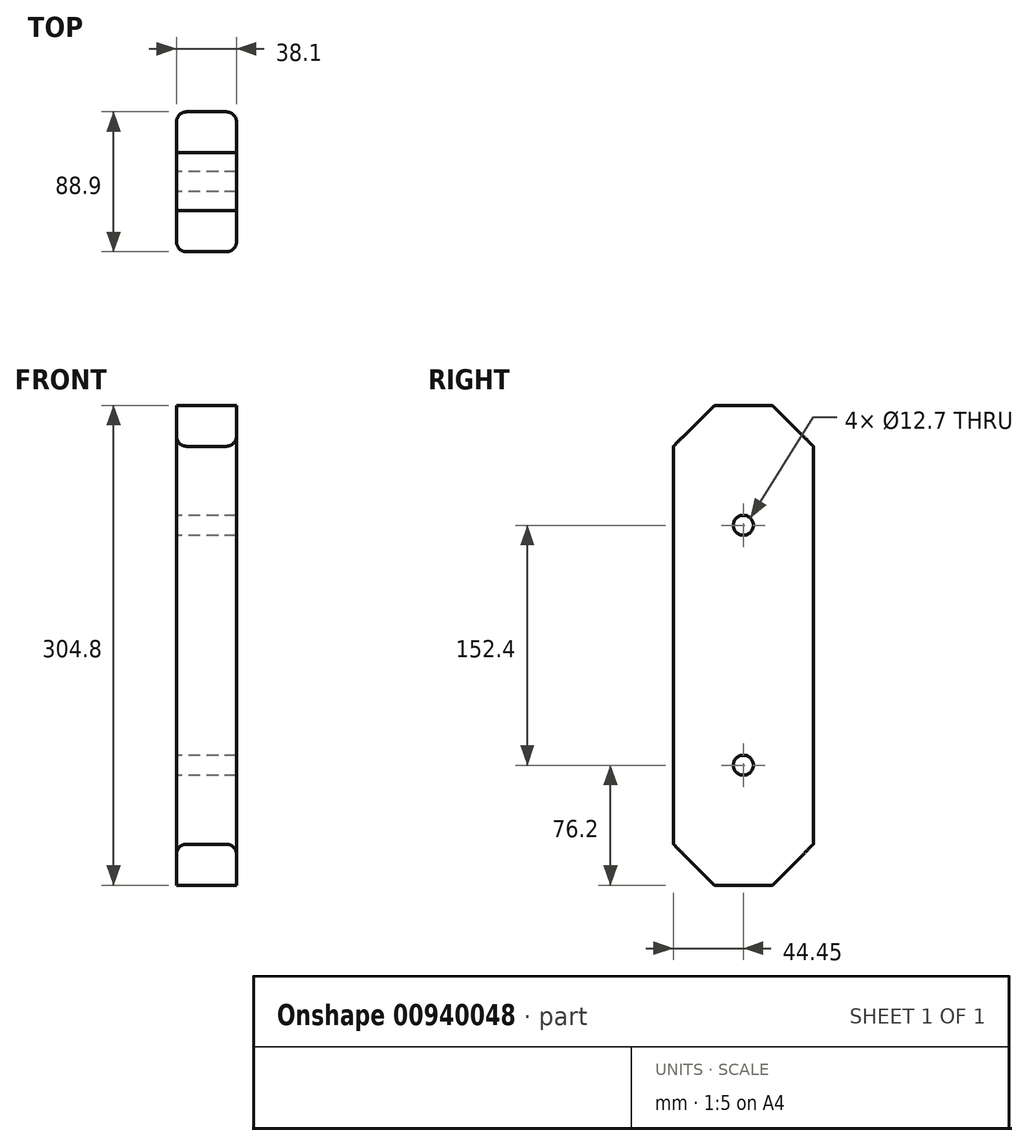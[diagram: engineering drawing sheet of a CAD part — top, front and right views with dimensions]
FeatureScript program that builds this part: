
annotation { "Feature Type Name" : "Feature", "Feature Type Description" : "" }
export const myFeature = defineFeature(function(context is Context, id is Id, definition is map)
    precondition{}
    {
        {
            var Q0;
            Q0=qCreatedBy(makeId("Top.planeOp"),FACE);
            var sketch = newSketch(context, id + "F0", { "sketchPlane" : qUnion([Q0])});
            skLineSegment(sketch, "E0.bottom", {"start": v(12.7, -44.45) * mm, "end": v(-12.7, -44.45) * mm});
            skLineSegment(sketch, "E0.top", {"start": v(12.7, 44.45) * mm, "end": v(-12.7, 44.45) * mm});
            skLineSegment(sketch, "E0.left", {"start": v(19.05, -38.1) * mm, "end": v(19.05, 38.1) * mm});
            skLineSegment(sketch, "E0.right", {"start": v(-19.05, -38.1) * mm, "end": v(-19.05, 38.1) * mm});
            skPoint(sketch, "E0.middle", {"position": v(0, 0) * mm});
            skPoint(sketch, "E1.visualSharp", {"position": v(19.05, -44.45) * mm});
            skArc(sketch, "E1.filletArc", {"start": v(12.7, -44.45) * mm, "mid": v(17.2, -42.6) * mm, "end": v(19.05, -38.1) * mm});
            skPoint(sketch, "E2.visualSharp", {"position": v(-19.05, -44.45) * mm});
            skArc(sketch, "E2.filletArc", {"start": v(-19.05, -38.1) * mm, "mid": v(-17.2, -42.6) * mm, "end": v(-12.7, -44.45) * mm});
            skPoint(sketch, "E3.visualSharp", {"position": v(-19.05, 44.45) * mm});
            skArc(sketch, "E3.filletArc", {"start": v(-12.7, 44.45) * mm, "mid": v(-17.2, 42.6) * mm, "end": v(-19.05, 38.1) * mm});
            skPoint(sketch, "E4.visualSharp", {"position": v(19.05, 44.45) * mm});
            skArc(sketch, "E4.filletArc", {"start": v(19.05, 38.1) * mm, "mid": v(17.2, 42.6) * mm, "end": v(12.7, 44.45) * mm});
            skSolve(sketch);
        }
        {
            var Q0;
            Q0 = qSketchRegion(id + "F0", true);
            extrude(context, id + "F1", {"entities" : qUnion([Q0]), "depth" : 304.8 * mm, "offsetDistance" : 25.4 * mm});
        }
        {
            var Q0;
            Q0=makeQuery(id+"F1.opExtrude","SWEPT_FACE",FACE,{"disambiguationData":[OSD([sQuery(id+"F0.wireOp",EDGE,"E0.right")])]});
            var sketch = newSketch(context, id + "F2", { "sketchPlane" : qUnion([Q0])});
            skLineSegment(sketch, "E5.0", {"start": v(-44.45, 304.8) * mm, "end": v(-44.45, 62.86) * mm});
            skLineSegment(sketch, "E6.0", {"start": v(44.45, 304.8) * mm, "end": v(44.45, 62.86) * mm});
            skLineSegment(sketch, "E7.0", {"start": v(38.1, 0) * mm, "end": v(-38.1, 0) * mm});
            skLineSegment(sketch, "E8.0", {"start": v(38.1, 0) * mm, "end": v(44.45, 0) * mm});
            skLineSegment(sketch, "E9.0", {"start": v(-44.45, 0) * mm, "end": v(-38.1, 0) * mm});
            skLineSegment(sketch, "E10.0", {"start": v(38.1, 304.8) * mm, "end": v(-38.1, 304.8) * mm});
            skLineSegment(sketch, "E11.0", {"start": v(38.1, 304.8) * mm, "end": v(44.45, 304.8) * mm});
            skLineSegment(sketch, "E12.0", {"start": v(-44.45, 304.8) * mm, "end": v(-38.1, 304.8) * mm});
            skPoint(sketch, "E13", {"position": v(0, 76.2) * mm});
            skLineSegment(sketch, "E14.0", {"start": v(18.41, 0) * mm, "end": v(-18.41, 0) * mm});
            skLineSegment(sketch, "E14.1", {"start": v(-18.41, 0) * mm, "end": v(-44.45, 26.04) * mm});
            skLineSegment(sketch, "E14.2", {"start": v(-44.45, 26.04) * mm, "end": v(-44.45, 62.86) * mm});
            skLineSegment(sketch, "E14.6", {"start": v(44.45, 62.86) * mm, "end": v(44.45, 26.04) * mm});
            skLineSegment(sketch, "E14.7", {"start": v(44.45, 26.04) * mm, "end": v(18.41, 0) * mm});
            skPoint(sketch, "E14.0.midPoint", {"position": v(0, 0) * mm});
            skLineSegment(sketch, "E15", {"start": v(-44.45, 152.4) * mm, "end": v(44.45, 152.4) * mm, "construction": true});
            skLineSegment(sketch, "E16.MirrorCS", {"start": v(44.45, 278.76) * mm, "end": v(18.41, 304.8) * mm});
            skLineSegment(sketch, "E17.MirrorCS", {"start": v(-18.41, 304.8) * mm, "end": v(-44.45, 278.76) * mm});
            skLineSegment(sketch, "E18.trimOffspring", {"start": v(44.45, 26.04) * mm, "end": v(44.45, 0) * mm});
            skLineSegment(sketch, "E19.trimOffspring", {"start": v(-44.45, 26.04) * mm, "end": v(-44.45, 0) * mm});
            skPoint(sketch, "E20.MirrorP", {"position": v(0, 228.6) * mm});
            skSolve(sketch);
        }
        {
            var Q0;
            {var subQ0=sQuery(id+"F2.wireOp",EDGE,"E12.0");Q0=makeQuery(id+"F2.imprint","IMPRINT",FACE,{"disambiguationData":[TD([[makeQuery(id+"F2.imprint","IMPRINT",EDGE,{"derivedFrom":subQ0}),-1.0]])]});}
            var Q1;
            {var subQ0=sQuery(id+"F2.wireOp",EDGE,"E11.0");Q1=makeQuery(id+"F2.imprint","IMPRINT",FACE,{"disambiguationData":[TD([[makeQuery(id+"F2.imprint","IMPRINT",EDGE,{"derivedFrom":subQ0}),-1.0]])]});}
            var Q2;
            {var subQ0=sQuery(id+"F2.wireOp",EDGE,"E7.0");var subQ3=sQuery(id+"F2.wireOp",EDGE,"E14.7");var subQ4=makeQuery(id+"F2.imprint","INTERSECT",VERTEX,{"derivedFrom":[subQ0,sQuery(id+"F2.wireOp",EDGE,"E14.0"),subQ3]});Q2=makeQuery(id+"F2.imprint","IMPRINT",FACE,{"disambiguationData":[TD([[makeQuery(id+"F2.imprint","IMPRINT",EDGE,{"disambiguationData":[TD([[subQ4,1.0]])],"derivedFrom":subQ3}),1.0]])]});}
            var Q3;
            {var subQ0=sQuery(id+"F2.wireOp",EDGE,"E7.0");var subQ3=sQuery(id+"F2.wireOp",EDGE,"E14.1");var subQ4=makeQuery(id+"F2.imprint","INTERSECT",VERTEX,{"derivedFrom":[subQ0,sQuery(id+"F2.wireOp",EDGE,"E14.0"),subQ3]});Q3=makeQuery(id+"F2.imprint","IMPRINT",FACE,{"disambiguationData":[TD([[makeQuery(id+"F2.imprint","IMPRINT",EDGE,{"disambiguationData":[TD([[subQ4,-1.0]])],"derivedFrom":subQ3}),1.0]])]});}
            var Q4;
            {var subQ0=sQuery(id+"F2.wireOp",EDGE,"E8.0");Q4=makeQuery(id+"F2.imprint","IMPRINT",FACE,{"disambiguationData":[TD([[makeQuery(id+"F2.imprint","IMPRINT",EDGE,{"derivedFrom":subQ0}),1.0]])]});}
            var Q5;
            {var subQ0=sQuery(id+"F2.wireOp",EDGE,"E9.0");Q5=makeQuery(id+"F2.imprint","IMPRINT",FACE,{"disambiguationData":[TD([[makeQuery(id+"F2.imprint","IMPRINT",EDGE,{"derivedFrom":subQ0}),1.0]])]});}
            var Q6;
            {var subQ0=sQuery(id+"F2.wireOp",EDGE,"E10.0");var subQ3=sQuery(id+"F2.wireOp",EDGE,"E16.MirrorCS");var subQ4=makeQuery(id+"F2.imprint","INTERSECT",VERTEX,{"derivedFrom":[subQ0,subQ3]});Q6=makeQuery(id+"F2.imprint","IMPRINT",FACE,{"disambiguationData":[TD([[makeQuery(id+"F2.imprint","IMPRINT",EDGE,{"disambiguationData":[TD([[subQ4,1.0]])],"derivedFrom":subQ3}),-1.0]])]});}
            var Q7;
            {var subQ0=sQuery(id+"F2.wireOp",EDGE,"E10.0");var subQ3=sQuery(id+"F2.wireOp",EDGE,"E17.MirrorCS");var subQ4=makeQuery(id+"F2.imprint","INTERSECT",VERTEX,{"derivedFrom":[subQ0,subQ3]});Q7=makeQuery(id+"F2.imprint","IMPRINT",FACE,{"disambiguationData":[TD([[makeQuery(id+"F2.imprint","IMPRINT",EDGE,{"disambiguationData":[TD([[subQ4,-1.0]])],"derivedFrom":subQ3}),-1.0]])]});}
            extrude(context, id + "F3", {"entities" : qUnion([Q0, Q1, Q2, Q3, Q4, Q5, Q6, Q7]), "operationType" : NewBodyOperationType.REMOVE, "oppositeDirection" : true, "depth" : 50.8 * mm, "offsetDistance" : 25.4 * mm});
        }
        {
            var Q0;
            Q0=sQuery(id+"F2.wireOp",VERTEX,"E13");
            var Q1;
            Q1=sQuery(id+"F2.wireOp",VERTEX,"E20.MirrorP");
            var Q2;
            Q2=makeQuery(id+"F1.opExtrude","SWEPT_BODY",BODY,{"disambiguationData":[OSD([sQuery(id+"F0.wireOp",EDGE,"E0.bottom"),sQuery(id+"F0.wireOp",EDGE,"E0.top"),sQuery(id+"F0.wireOp",EDGE,"E0.left"),sQuery(id+"F0.wireOp",EDGE,"E0.right"),sQuery(id+"F0.wireOp",EDGE,"E1.filletArc"),sQuery(id+"F0.wireOp",EDGE,"E2.filletArc"),sQuery(id+"F0.wireOp",EDGE,"E3.filletArc"),sQuery(id+"F0.wireOp",EDGE,"E4.filletArc")])]});
            hole(context, id + "F4", {"style" : HoleStyle.SIMPLE, "endStyle" : HoleEndStyle.THROUGH, "holeDiameter" : 12.7 * mm, "majorDiameter" : 6.35 * mm, "isTappedThrough" : true, "tappedDepth" : 12.7 * mm, "tapClearance" : 3, "locations" : qUnion([Q0, Q1]), "scope" : qUnion([Q2])});
        }
    });
